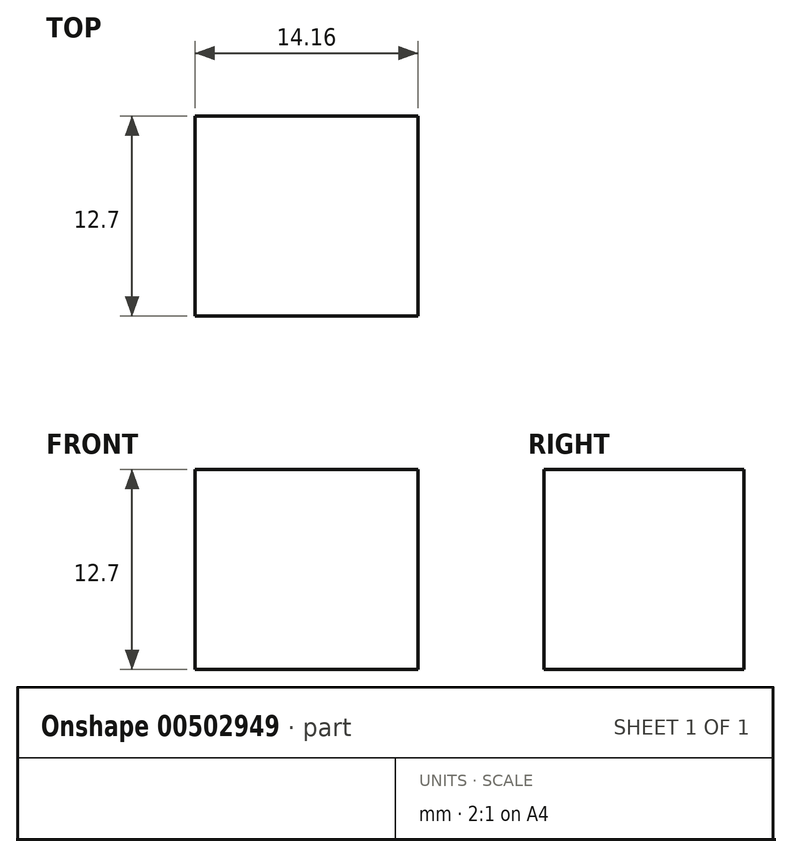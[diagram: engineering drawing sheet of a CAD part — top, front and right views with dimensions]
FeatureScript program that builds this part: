
annotation { "Feature Type Name" : "Feature", "Feature Type Description" : "" }
export const myFeature = defineFeature(function(context is Context, id is Id, definition is map)
    precondition{}
    {
        {
            var Q0;
            Q0=qCreatedBy(makeId("Top.planeOp"),FACE);
            var sketch = newSketch(context, id + "F0", { "sketchPlane" : qUnion([Q0])});
            skLineSegment(sketch, "E0.bottom", {"start": v(0, 0) * mm, "end": v(14.16, 0) * mm});
            skLineSegment(sketch, "E0.top", {"start": v(0, 12.7) * mm, "end": v(14.16, 12.7) * mm});
            skLineSegment(sketch, "E0.left", {"start": v(0, 0) * mm, "end": v(0, 12.7) * mm});
            skLineSegment(sketch, "E0.right", {"start": v(14.16, 0) * mm, "end": v(14.16, 12.7) * mm});
            skSolve(sketch);
        }
        {
            var Q0;
            Q0=makeQuery(id+"F0.imprint","IMPRINT",FACE,{"disambiguationData":[TD([[makeQuery(id+"F0.imprint","IMPRINT",EDGE,{"derivedFrom":sQuery(id+"F0.wireOp",EDGE,"E0.bottom")}),1.0]])]});
            extrude(context, id + "F1", {"entities" : qUnion([Q0]), "depth" : 12.7 * mm});
        }
    });
